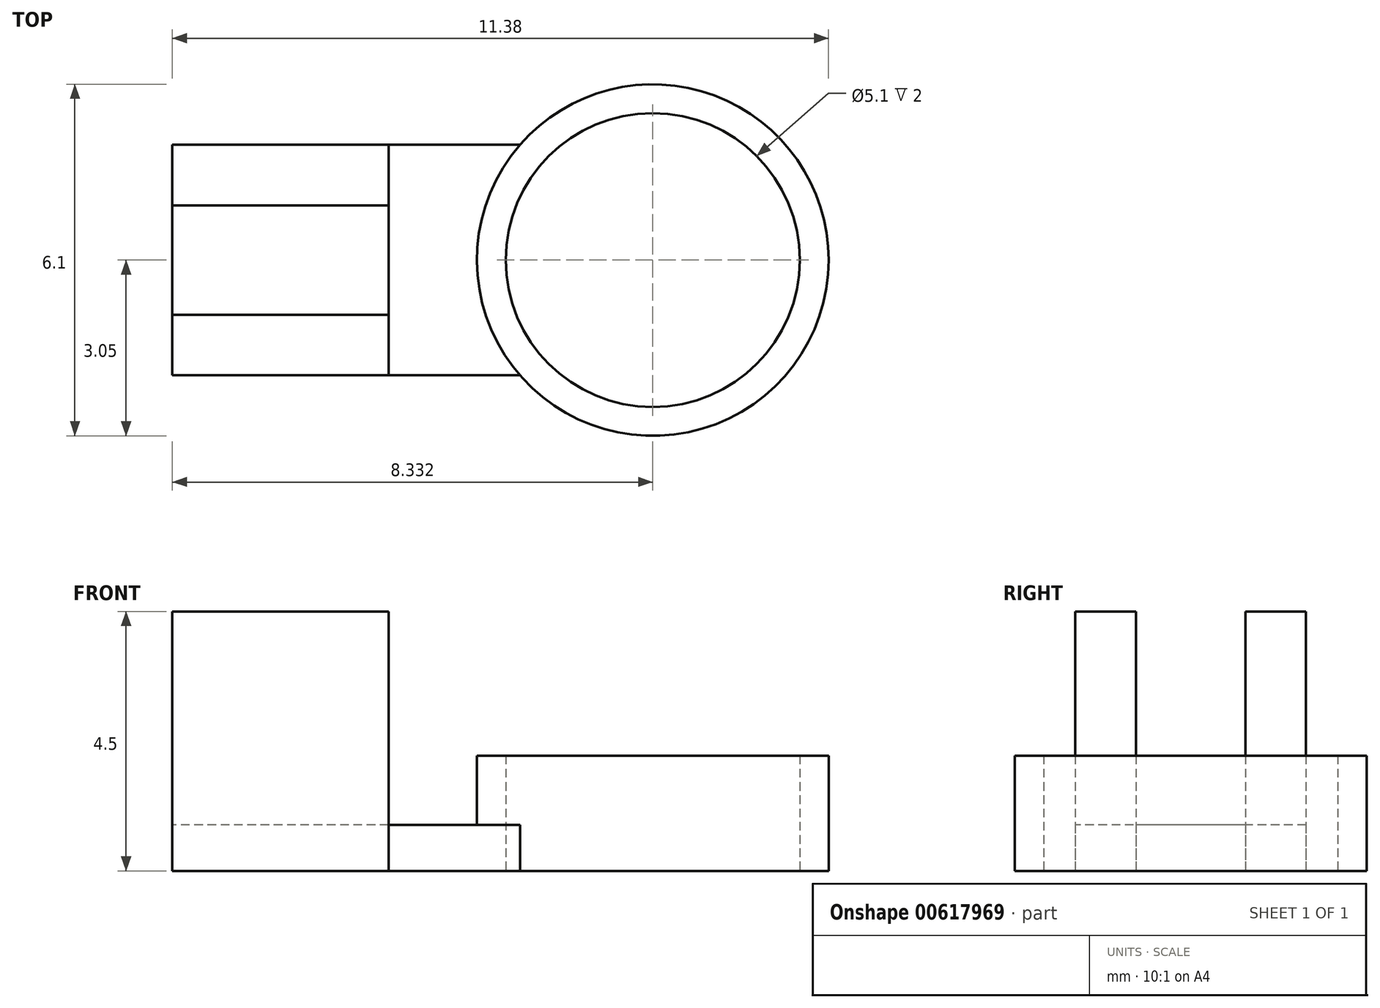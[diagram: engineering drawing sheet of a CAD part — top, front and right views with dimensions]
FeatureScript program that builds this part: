
annotation { "Feature Type Name" : "Feature", "Feature Type Description" : "" }
export const myFeature = defineFeature(function(context is Context, id is Id, definition is map)
    precondition{}
    {
        {
            var Q0;
            Q0=qCreatedBy(makeId("Top.planeOp"),FACE);
            var sketch = newSketch(context, id + "F0", { "sketchPlane" : qUnion([Q0])});
            skLineSegment(sketch, "E0", {"start": v(0, 0) * mm, "end": v(-3.75, 0) * mm});
            skLineSegment(sketch, "E1", {"start": v(-3.75, 4) * mm, "end": v(0, 4) * mm});
            skLineSegment(sketch, "E2", {"start": v(0, 4) * mm, "end": v(0, 2.95) * mm});
            skLineSegment(sketch, "E3", {"start": v(0, 2.95) * mm, "end": v(-3.75, 2.95) * mm});
            skLineSegment(sketch, "E4", {"start": v(-3.75, 1.05) * mm, "end": v(0, 1.05) * mm});
            skLineSegment(sketch, "E5", {"start": v(0, 1.05) * mm, "end": v(0, 0) * mm});
            skLineSegment(sketch, "E6", {"start": v(-3.75, 4) * mm, "end": v(-3.75, 2.95) * mm});
            skLineSegment(sketch, "E7", {"start": v(-3.75, 1.05) * mm, "end": v(-3.75, 0) * mm});
            skLineSegment(sketch, "E8.top", {"start": v(-3.75, 0) * mm, "end": v(0, 0) * mm});
            skLineSegment(sketch, "E8.left", {"start": v(-3.75, 4) * mm, "end": v(-3.75, 0) * mm});
            skLineSegment(sketch, "E9", {"start": v(0, 4) * mm, "end": v(3, 4) * mm});
            skLineSegment(sketch, "E10", {"start": v(0, 0) * mm, "end": v(3, 0) * mm});
            skLineSegment(sketch, "E11", {"start": v(0, 4) * mm, "end": v(0, 0) * mm});
            skCircle(sketch, "E12", {"center": v(4.58, 2) * mm, "radius": 2.55 * mm});
            skArc(sketch, "E13", {"start": v(3, 4) * mm, "mid": v(2.03, 2) * mm, "end": v(3, 0) * mm});
            skCircle(sketch, "E14", {"center": v(4.58, 2) * mm, "radius": 3.05 * mm});
            skSolve(sketch);
        }
        {
            var Q0;
            {var subQ0=sQuery(id+"F0.wireOp",EDGE,"E3");Q0=makeQuery(id+"F0.imprint","IMPRINT",FACE,{"disambiguationData":[TD([[makeQuery(id+"F0.imprint","IMPRINT",EDGE,{"derivedFrom":subQ0}),-1.0]])]});}
            var Q1;
            {var subQ0=sQuery(id+"F0.wireOp",EDGE,"E4");Q1=makeQuery(id+"F0.imprint","IMPRINT",FACE,{"disambiguationData":[TD([[makeQuery(id+"F0.imprint","IMPRINT",EDGE,{"derivedFrom":subQ0}),-1.0]])]});}
            extrude(context, id + "F1", {"entities" : qUnion([Q0, Q1]), "depth" : 4.5 * mm, "offsetDistance" : 25 * mm});
        }
        {
            var Q0;
            {var subQ0=sQuery(id+"F0.wireOp",EDGE,"E3");Q0=makeQuery(id+"F0.imprint","IMPRINT",FACE,{"disambiguationData":[TD([[makeQuery(id+"F0.imprint","IMPRINT",EDGE,{"derivedFrom":subQ0}),1.0]])]});}
            extrude(context, id + "F2", {"entities" : qUnion([Q0]), "depth" : .8 * mm, "offsetDistance" : 25 * mm});
        }
        {
            var Q0;
            {var subQ0=sQuery(id+"F0.wireOp",EDGE,"E11");var subQ1=makeQuery(id+"F0.imprint","INTERSECT",VERTEX,{"derivedFrom":[sQuery(id+"F0.wireOp",EDGE,"E3"),subQ0]});Q0=makeQuery(id+"F0.imprint","IMPRINT",FACE,{"disambiguationData":[TD([[makeQuery(id+"F0.imprint","IMPRINT",EDGE,{"disambiguationData":[TD([[subQ1,-1.0]])],"derivedFrom":subQ0}),1.0]])]});}
            extrude(context, id + "F3", {"entities" : qUnion([Q0]), "depth" : .8 * mm, "offsetDistance" : 25 * mm});
        }
        {
            var Q0;
            {var subQ0=sQuery(id+"F0.wireOp",EDGE,"E12");var subQ1=sQuery(id+"F0.wireOp",EDGE,"E9");var subQ2=makeQuery(id+"F0.imprint","INTERSECT",VERTEX,{"derivedFrom":[subQ1,subQ0]});Q0=makeQuery(id+"F0.imprint","IMPRINT",FACE,{"disambiguationData":[TD([[makeQuery(id+"F0.imprint","IMPRINT",EDGE,{"disambiguationData":[TD([[subQ2,1.0]])],"derivedFrom":subQ1}),1.0]])]});}
            var Q1;
            {var subQ0=sQuery(id+"F0.wireOp",EDGE,"E12");var subQ1=sQuery(id+"F0.wireOp",EDGE,"E9");var subQ2=makeQuery(id+"F0.imprint","INTERSECT",VERTEX,{"derivedFrom":[subQ1,subQ0]});Q1=makeQuery(id+"F0.imprint","IMPRINT",FACE,{"disambiguationData":[TD([[makeQuery(id+"F0.imprint","IMPRINT",EDGE,{"disambiguationData":[TD([[subQ2,1.0]])],"derivedFrom":subQ1}),-1.0]])]});}
            extrude(context, id + "F4", {"entities" : qUnion([Q0, Q1]), "operationType" : NewBodyOperationType.ADD, "depth" : 2 * mm, "offsetDistance" : 25 * mm});
        }
    });
